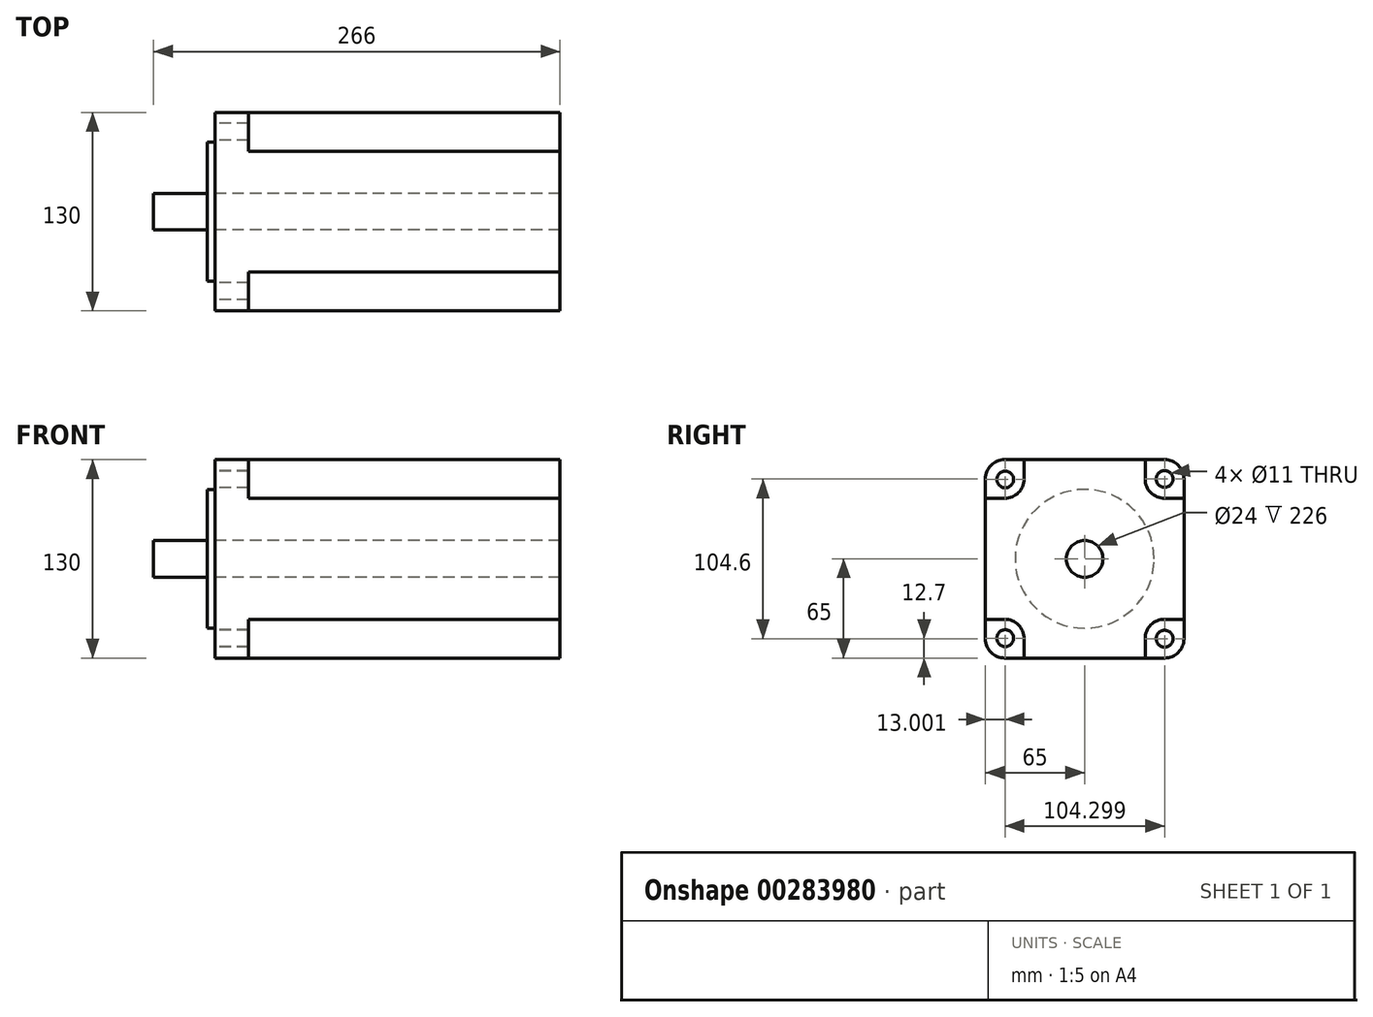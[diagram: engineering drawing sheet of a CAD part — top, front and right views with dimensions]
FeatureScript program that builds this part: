
annotation { "Feature Type Name" : "Feature", "Feature Type Description" : "" }
export const myFeature = defineFeature(function(context is Context, id is Id, definition is map)
    precondition{}
    {
        {
            var Q0;
            Q0=qCreatedBy(makeId("Right.planeOp"),FACE);
            var sketch = newSketch(context, id + "F0", { "sketchPlane" : qUnion([Q0])});
            skLineSegment(sketch, "E0.bottom", {"start": v(52.3, -65) * mm, "end": v(-52.3, -65) * mm});
            skLineSegment(sketch, "E0.top", {"start": v(52.3, 65) * mm, "end": v(-52.3, 65) * mm});
            skLineSegment(sketch, "E0.left", {"start": v(65, -52.3) * mm, "end": v(65, 52.3) * mm});
            skLineSegment(sketch, "E0.right", {"start": v(-65, -52.3) * mm, "end": v(-65, 52.3) * mm});
            skPoint(sketch, "E0.middle", {"position": v(0, 0) * mm});
            skCircle(sketch, "E1", {"center": v(0, 0) * mm, "radius": 12 * mm});
            skPoint(sketch, "E2.visualSharp", {"position": v(-65, 65) * mm});
            skArc(sketch, "E2.filletArc", {"start": v(-52.3, 65) * mm, "mid": v(-61.28, 61.28) * mm, "end": v(-65, 52.3) * mm});
            skPoint(sketch, "E3.visualSharp", {"position": v(65, 65) * mm});
            skArc(sketch, "E3.filletArc", {"start": v(65, 52.3) * mm, "mid": v(61.28, 61.28) * mm, "end": v(52.3, 65) * mm});
            skPoint(sketch, "E4.visualSharp", {"position": v(65, -65) * mm});
            skArc(sketch, "E4.filletArc", {"start": v(52.3, -65) * mm, "mid": v(61.28, -61.28) * mm, "end": v(65, -52.3) * mm});
            skPoint(sketch, "E5.visualSharp", {"position": v(-65, -65) * mm});
            skArc(sketch, "E5.filletArc", {"start": v(-65, -52.3) * mm, "mid": v(-61.28, -61.28) * mm, "end": v(-52.3, -65) * mm});
            skPoint(sketch, "E6.visualSharp", {"position": v(-52, 52) * mm});
            skPoint(sketch, "E7.visualSharp", {"position": v(52, 52) * mm});
            skPoint(sketch, "E8.visualSharp", {"position": v(52, -52) * mm});
            skPoint(sketch, "E9.visualSharp", {"position": v(-52, -52) * mm});
            skCircle(sketch, "E10", {"center": v(0, 0) * mm, "radius": 45.5 * mm});
            skLineSegment(sketch, "E11", {"start": v(-39.6, -65) * mm, "end": v(-39.6, -52.3) * mm});
            skLineSegment(sketch, "E12", {"start": v(-52.3, -39.6) * mm, "end": v(-65, -39.6) * mm});
            skLineSegment(sketch, "E13", {"start": v(-39.6, 65) * mm, "end": v(-39.6, 52.3) * mm});
            skLineSegment(sketch, "E14", {"start": v(-52.3, 39.6) * mm, "end": v(-65, 39.6) * mm});
            skLineSegment(sketch, "E15", {"start": v(39.6, 65) * mm, "end": v(39.6, 52.3) * mm});
            skLineSegment(sketch, "E16", {"start": v(52.3, 39.6) * mm, "end": v(65, 39.6) * mm});
            skLineSegment(sketch, "E17", {"start": v(39.6, -65) * mm, "end": v(39.6, -52.3) * mm});
            skLineSegment(sketch, "E18", {"start": v(52.3, -39.6) * mm, "end": v(65, -39.6) * mm});
            skCircle(sketch, "E19", {"center": v(-52, 52) * mm, "radius": 5.5 * mm});
            skCircle(sketch, "E20", {"center": v(52.3, 52.3) * mm, "radius": 5.5 * mm});
            skCircle(sketch, "E21", {"center": v(52.3, -52.3) * mm, "radius": 5.5 * mm});
            skCircle(sketch, "E22", {"center": v(-52, -52) * mm, "radius": 5.5 * mm});
            skPoint(sketch, "E23.visualSharp", {"position": v(-39.6, 39.6) * mm});
            skArc(sketch, "E23.filletArc", {"start": v(-52.3, 39.6) * mm, "mid": v(-43.32, 43.32) * mm, "end": v(-39.6, 52.3) * mm});
            skPoint(sketch, "E24.visualSharp", {"position": v(39.6, 39.6) * mm});
            skArc(sketch, "E24.filletArc", {"start": v(39.6, 52.3) * mm, "mid": v(43.32, 43.32) * mm, "end": v(52.3, 39.6) * mm});
            skPoint(sketch, "E25.visualSharp", {"position": v(39.6, -39.6) * mm});
            skArc(sketch, "E25.filletArc", {"start": v(52.3, -39.6) * mm, "mid": v(43.32, -43.32) * mm, "end": v(39.6, -52.3) * mm});
            skPoint(sketch, "E26.visualSharp", {"position": v(-39.6, -39.6) * mm});
            skArc(sketch, "E26.filletArc", {"start": v(-39.6, -52.3) * mm, "mid": v(-43.32, -43.32) * mm, "end": v(-52.3, -39.6) * mm});
            skSolve(sketch);
        }
        {
            var Q0;
            Q0=makeQuery(id+"F0.imprint","IMPRINT",FACE,{"disambiguationData":[TD([[makeQuery(id+"F0.imprint","IMPRINT",EDGE,{"derivedFrom":sQuery(id+"F0.wireOp",EDGE,"E1")}),1.0]])]});
            extrude(context, id + "F1", {"entities" : qUnion([Q0]), "oppositeDirection" : true, "depth" : 40 * mm});
        }
        {
            var Q0;
            Q0=makeQuery(id+"F0.imprint","IMPRINT",FACE,{"disambiguationData":[TD([[makeQuery(id+"F0.imprint","IMPRINT",EDGE,{"derivedFrom":sQuery(id+"F0.wireOp",EDGE,"E1")}),-1.0]])]});
            extrude(context, id + "F2", {"entities" : qUnion([Q0]), "operationType" : NewBodyOperationType.ADD, "oppositeDirection" : true, "depth" : 0.12 * 40 * mm});
        }
        {
            var Q0;
            Q0=makeQuery(id+"F0.imprint","IMPRINT",FACE,{"disambiguationData":[TD([[makeQuery(id+"F0.imprint","IMPRINT",EDGE,{"derivedFrom":sQuery(id+"F0.wireOp",EDGE,"E1")}),-1.0]])]});
            var Q1;
            Q1=makeQuery(id+"F0.imprint","IMPRINT",FACE,{"disambiguationData":[TD([[makeQuery(id+"F0.imprint","IMPRINT",EDGE,{"derivedFrom":sQuery(id+"F0.wireOp",EDGE,"E10")}),-1.0]])]});
            extrude(context, id + "F3", {"entities" : qUnion([Q0, Q1]), "operationType" : NewBodyOperationType.ADD, "depth" : 226 * mm});
        }
        {
            var Q0;
            {var subQ0=sQuery(id+"F0.wireOp",EDGE,"E2.filletArc");Q0=makeQuery(id+"F0.imprint","IMPRINT",FACE,{"disambiguationData":[TD([[makeQuery(id+"F0.imprint","IMPRINT",EDGE,{"derivedFrom":subQ0}),1.0]])]});}
            var Q1;
            {var subQ1=sQuery(id+"F0.wireOp",EDGE,"E3.filletArc");Q1=makeQuery(id+"F0.imprint","IMPRINT",FACE,{"disambiguationData":[TD([[makeQuery(id+"F0.imprint","IMPRINT",EDGE,{"derivedFrom":subQ1}),1.0]])]});}
            var Q2;
            {var subQ1=sQuery(id+"F0.wireOp",EDGE,"E4.filletArc");Q2=makeQuery(id+"F0.imprint","IMPRINT",FACE,{"disambiguationData":[TD([[makeQuery(id+"F0.imprint","IMPRINT",EDGE,{"derivedFrom":subQ1}),1.0]])]});}
            var Q3;
            {var subQ1=sQuery(id+"F0.wireOp",EDGE,"E5.filletArc");Q3=makeQuery(id+"F0.imprint","IMPRINT",FACE,{"disambiguationData":[TD([[makeQuery(id+"F0.imprint","IMPRINT",EDGE,{"derivedFrom":subQ1}),1.0]])]});}
            extrude(context, id + "F4", {"entities" : qUnion([Q0, Q1, Q2, Q3]), "operationType" : NewBodyOperationType.ADD, "depth" : 2 * 11 * mm});
        }
    });
